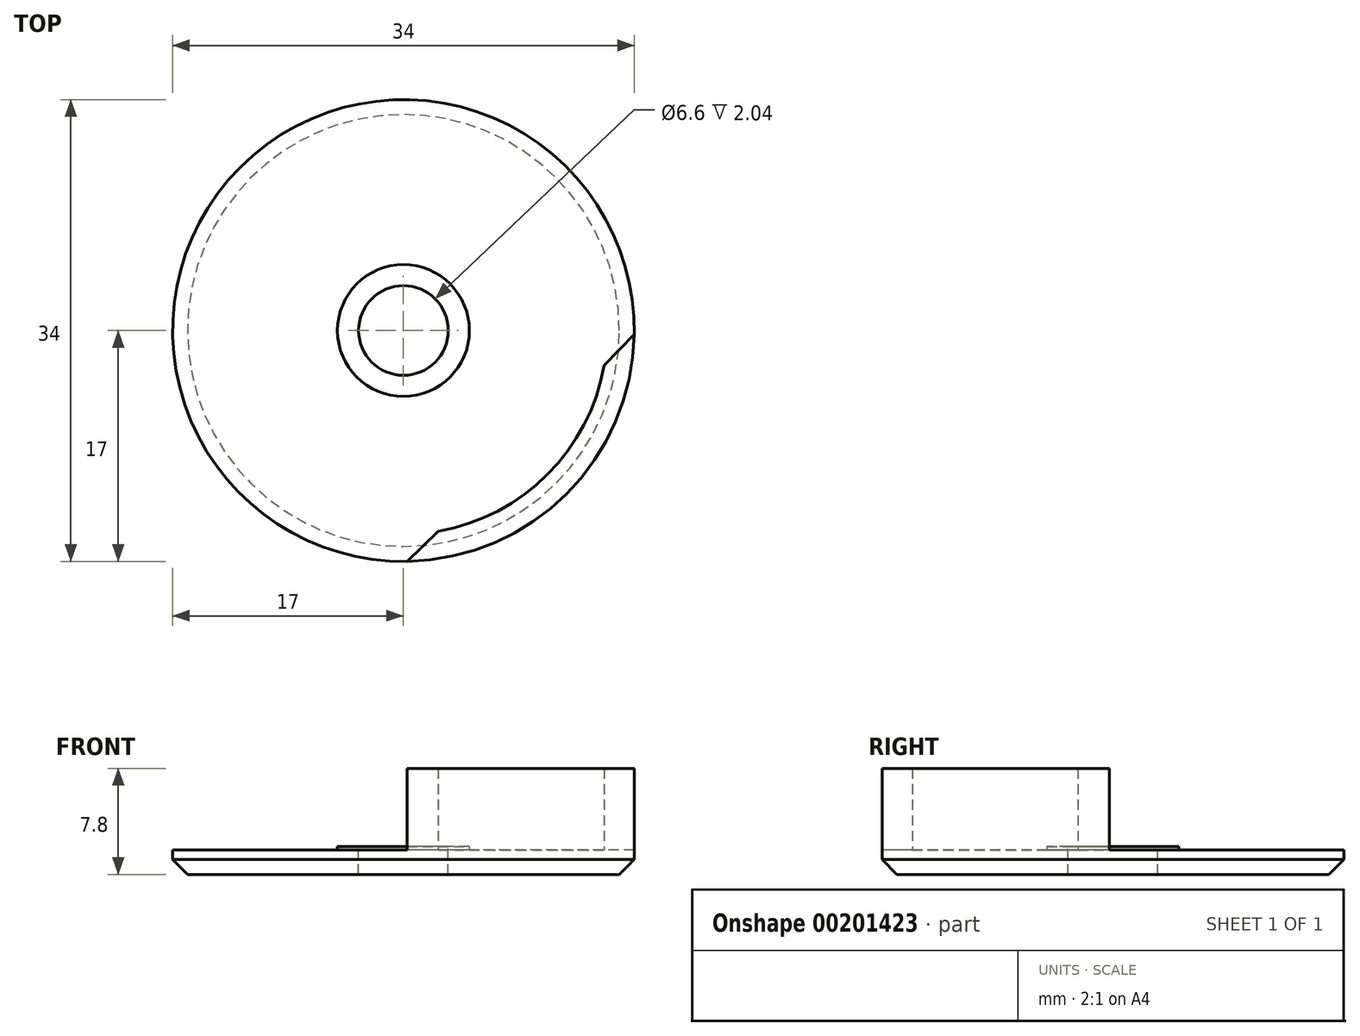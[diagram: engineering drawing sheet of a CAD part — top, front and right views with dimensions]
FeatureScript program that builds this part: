
annotation { "Feature Type Name" : "Feature", "Feature Type Description" : "" }
export const myFeature = defineFeature(function(context is Context, id is Id, definition is map)
    precondition{}
    {
        {
            var Q0;
            Q0=qCreatedBy(makeId("Top.planeOp"),FACE);
            var sketch = newSketch(context, id + "F0", { "sketchPlane" : qUnion([Q0])});
            skCircle(sketch, "E0", {"center": v(0, 0) * mm, "radius": 17 * mm});
            skSolve(sketch);
        }
        {
            var Q0;
            Q0=makeQuery(id+"F0.imprint","IMPRINT",FACE,{"disambiguationData":[TD([[makeQuery(id+"F0.imprint","IMPRINT",EDGE,{"derivedFrom":sQuery(id+"F0.wireOp",EDGE,"E0")}),1.0]])]});
            extrude(context, id + "F1", {"entities" : qUnion([Q0]), "depth" : 1.8 * mm});
        }
        {
            var Q0;
            Q0=makeQuery(id+"F1.opExtrude","CAP_FACE",FACE,{"disambiguationData":[OSD([sQuery(id+"F0.wireOp",EDGE,"E0")])],"isStart":false});
            var sketch = newSketch(context, id + "F2", { "sketchPlane" : qUnion([Q0])});
            skPoint(sketch, "E1", {"position": v(0, 0) * mm});
            skSolve(sketch);
        }
        {
            var Q0;
            Q0=sQuery(id+"F2.wireOp",VERTEX,"E1");
            var Q1;
            Q1=makeQuery(id+"F1.opExtrude","SWEPT_BODY",BODY,{"disambiguationData":[OSD([sQuery(id+"F0.wireOp",EDGE,"E0")])]});
            hole(context, id + "F3", {"style" : HoleStyle.SIMPLE, "endStyle" : HoleEndStyle.THROUGH, "standardTappedOrClearance" : lookupTablePath({ "standard" : "ISO", "fit" : "Normal", "size" : "M6", "type" : "Clearance" }), "standardBlindInLast" : lookupTablePath({ "fit" : "Standard", "standard" : "ISO", "size" : "M6", "type" : "Clearance" }), "holeDiameter" : 6.6 * mm, "startFromSketch" : true, "locations" : qUnion([Q0]), "scope" : qUnion([Q1]), "isTappedThrough" : true});
        }
        {
            var Q0;
            Q0=makeQuery(id+"F1.opExtrude","CAP_FACE",FACE,{"disambiguationData":[OSD([sQuery(id+"F0.wireOp",EDGE,"E0")])],"isStart":false});
            var sketch = newSketch(context, id + "F4", { "sketchPlane" : qUnion([Q0])});
            skArc(sketch, "E2", {"start": v(17, 0) * mm, "mid": v(12.02, -12.02) * mm, "end": v(0, -17) * mm});
            skArc(sketch, "E3.0", {"start": v(15, 0) * mm, "mid": v(10.6, -10.6) * mm, "end": v(0, -15) * mm});
            skLineSegment(sketch, "E4", {"start": v(0, -15) * mm, "end": v(0, -17) * mm});
            skLineSegment(sketch, "E5", {"start": v(15, 0) * mm, "end": v(17, 0) * mm});
            skSolve(sketch);
        }
        {
            var Q0;
            Q0=makeQuery(id+"F4.imprint","IMPRINT",FACE,{"disambiguationData":[TD([[makeQuery(id+"F4.imprint","IMPRINT",EDGE,{"derivedFrom":sQuery(id+"F4.wireOp",EDGE,"E2")}),1.0]])]});
            extrude(context, id + "F5", {"entities" : qUnion([Q0]), "operationType" : NewBodyOperationType.ADD, "depth" : 6 * mm});
        }
        {
            var Q0;
            Q0=makeQuery(id+"F5.opExtrude","SWEPT_EDGE",EDGE,{"disambiguationData":[OSD([sQuery(id+"F4.wireOp",EDGE,"E3.0"),sQuery(id+"F4.wireOp",EDGE,"E4")])]});
            var Q1;
            Q1=makeQuery(id+"F5.opExtrude","SWEPT_EDGE",EDGE,{"disambiguationData":[OSD([sQuery(id+"F4.wireOp",EDGE,"E3.0"),sQuery(id+"F4.wireOp",EDGE,"E5")])]});
            chamfer(context, id + "F6", {"entities" : qUnion([Q0, Q1]), "chamferType" : ChamferType.OFFSET_ANGLE, "width" : 3 * mm, "oppositeDirection" : true, "angle" : 40 * degree, "tangentPropagation" : true});
        }
        {
            var Q0;
            Q0=makeQuery(id+"F1.opExtrude","CAP_EDGE",EDGE,{"disambiguationData":[OSD([sQuery(id+"F0.wireOp",EDGE,"E0")])],"isStart":true});
            chamfer(context, id + "F7", {"entities" : qUnion([Q0]), "width" : 1.1 * mm, "tangentPropagation" : true});
        }
        {
            var Q0;
            Q0=makeQuery(id+"F1.opExtrude","CAP_FACE",FACE,{"disambiguationData":[OSD([sQuery(id+"F0.wireOp",EDGE,"E0")])],"isStart":false});
            var sketch = newSketch(context, id + "F8", { "sketchPlane" : qUnion([Q0])});
            skCircle(sketch, "E6", {"center": v(0, 0) * mm, "radius": 4.86 * mm});
            skSolve(sketch);
        }
        {
            var Q0;
            Q0=makeQuery(id+"F8.imprint","IMPRINT",FACE,{"disambiguationData":[TD([[makeQuery(id+"F8.imprint","IMPRINT",EDGE,{"derivedFrom":sQuery(id+"F8.wireOp",EDGE,"E6")}),1.0]])]});
            extrude(context, id + "F9", {"entities" : qUnion([Q0]), "operationType" : NewBodyOperationType.ADD, "depth" : 0.24 * mm});
        }
    });
